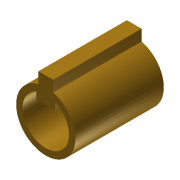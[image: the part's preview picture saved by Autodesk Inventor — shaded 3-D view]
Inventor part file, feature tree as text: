
AUTODESK INVENTOR PART (.ipt)
format: ipt  version: 2011 (Build 150239000, 239)  size: 99,328 bytes
history: native  units: in
note: dims shown in document units (in); Inventor stores cm internally (conversion verified against a paired STEP export)
features: extrude x1, sketch x1
ambient origin geometry x8: Origin, YZ Plane, XZ Plane, XY Plane, X Axis, Y Axis, Z Axis, Center Point
bodies: Solid1 (feature_tree)
feature tree (2):
  extrude  "Extrusion1"  [1 undecoded]
  sketch  "Sketch1"  dims[d0=0.75in d1=0.0in]
note: 1 required parameter value undecoded (feature->parameter linkage not recoverable at this tier; creation-order binding heuristic only, values carry confidence <= 0.55)
